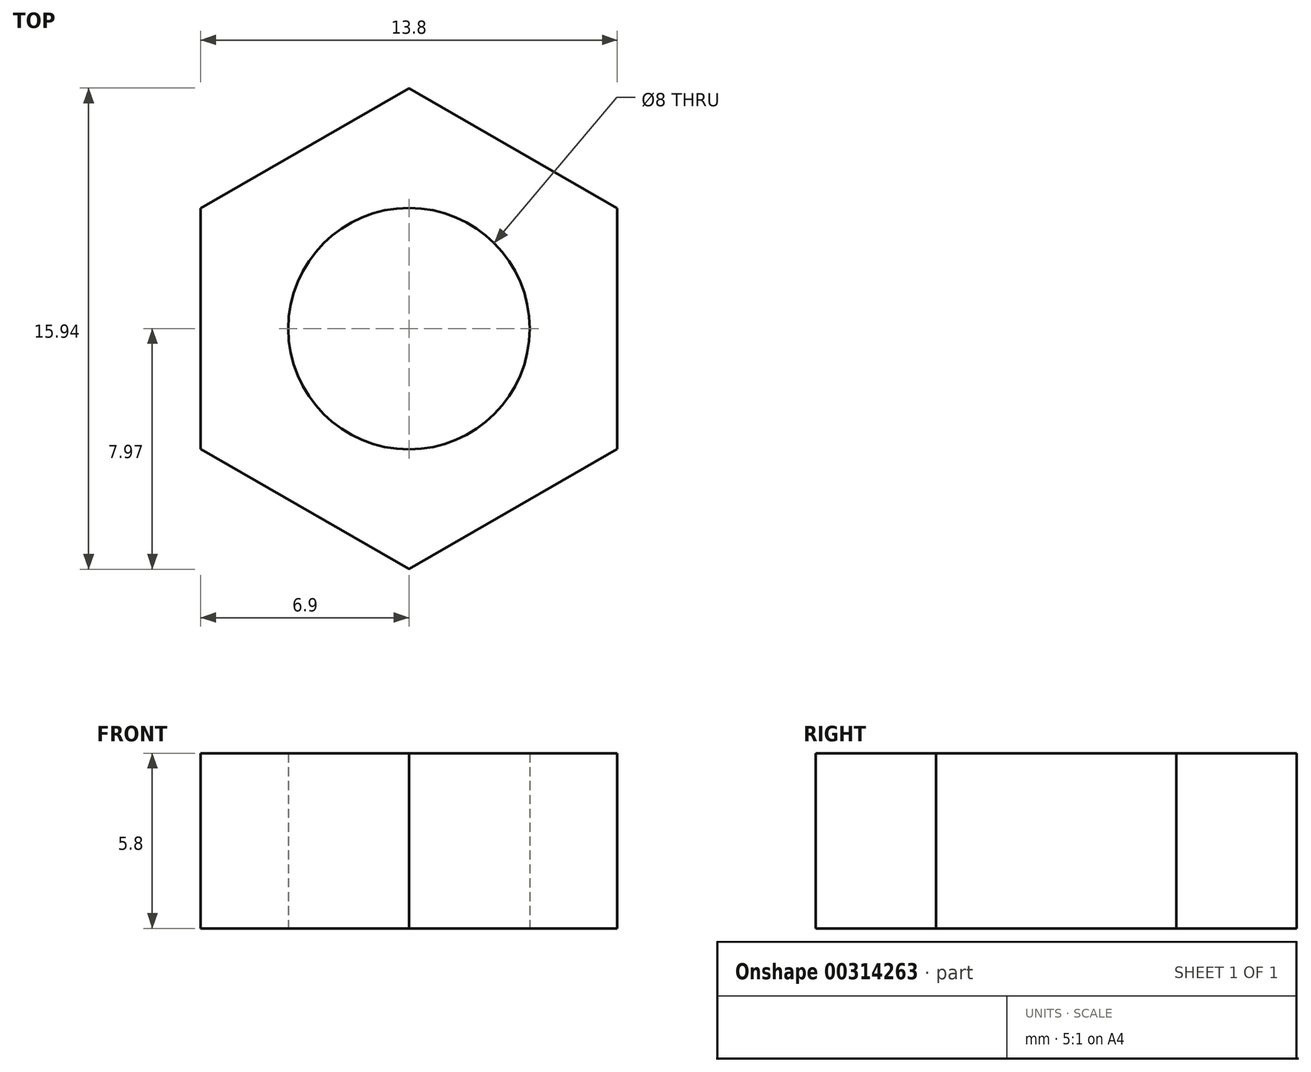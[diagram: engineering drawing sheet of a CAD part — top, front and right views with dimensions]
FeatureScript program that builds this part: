
annotation { "Feature Type Name" : "Feature", "Feature Type Description" : "" }
export const myFeature = defineFeature(function(context is Context, id is Id, definition is map)
    precondition{}
    {
        {
            var Q0;
            Q0=qCreatedBy(makeId("Top.planeOp"),FACE);
            var sketch = newSketch(context, id + "F0", { "sketchPlane" : qUnion([Q0])});
            skCircle(sketch, "E0", {"center": v(0, 0) * mm, "radius": 4 * mm});
            skCircle(sketch, "E1.cCircle", {"center": v(0, 0) * mm, "radius": 6.9 * mm, "construction": true});
            skLineSegment(sketch, "E1.0", {"start": v(6.9, 3.98) * mm, "end": v(6.9, -3.98) * mm});
            skLineSegment(sketch, "E1.1", {"start": v(6.9, -3.98) * mm, "end": v(0, -7.97) * mm});
            skLineSegment(sketch, "E1.2", {"start": v(0, -7.97) * mm, "end": v(-6.9, -3.98) * mm});
            skLineSegment(sketch, "E1.3", {"start": v(-6.9, -3.98) * mm, "end": v(-6.9, 3.98) * mm});
            skLineSegment(sketch, "E1.4", {"start": v(-6.9, 3.98) * mm, "end": v(0, 7.97) * mm});
            skLineSegment(sketch, "E1.5", {"start": v(0, 7.97) * mm, "end": v(6.9, 3.98) * mm});
            skPoint(sketch, "E1.0.midPoint", {"position": v(6.9, 0) * mm});
            skSolve(sketch);
        }
        {
            var Q0;
            Q0 = qSketchRegion(id + "F0", true);
            extrude(context, id + "F1", {"entities" : qUnion([Q0]), "depth" : 5.8 * mm});
        }
    });
